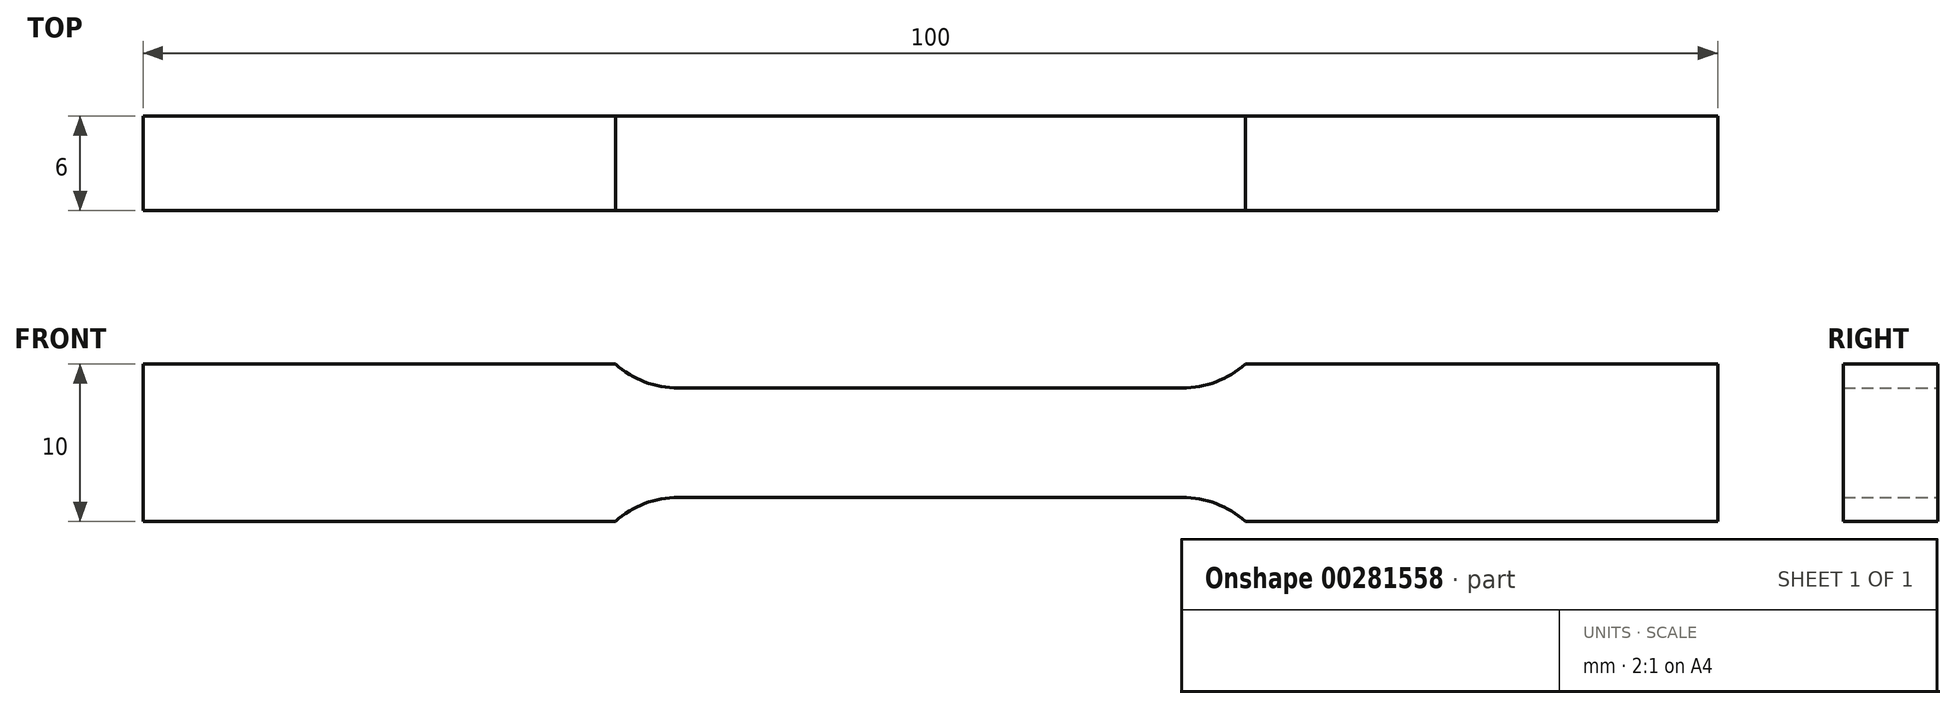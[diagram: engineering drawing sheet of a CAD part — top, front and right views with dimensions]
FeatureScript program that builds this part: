
annotation { "Feature Type Name" : "Feature", "Feature Type Description" : "" }
export const myFeature = defineFeature(function(context is Context, id is Id, definition is map)
    precondition{}
    {
        {
            var Q0;
            Q0=qCreatedBy(makeId("Front.planeOp"),FACE);
            var sketch = newSketch(context, id + "F0", { "sketchPlane" : qUnion([Q0])});
            skLineSegment(sketch, "E0", {"start": v(0, 3.47) * mm, "end": v(16, 3.47) * mm});
            skArc(sketch, "E1", {"start": v(16, 3.47) * mm, "mid": v(18.14, 3.87) * mm, "end": v(20, 5) * mm});
            skLineSegment(sketch, "E2", {"start": v(20, 5) * mm, "end": v(50, 5) * mm});
            skLineSegment(sketch, "E3", {"start": v(50, 5) * mm, "end": v(50, 0) * mm});
            skLineSegment(sketch, "E4.MirrorCS", {"start": v(0, -3.47) * mm, "end": v(16, -3.47) * mm});
            skLineSegment(sketch, "E5.MirrorCS", {"start": v(50, -5) * mm, "end": v(50, 0) * mm});
            skLineSegment(sketch, "E6.MirrorCS", {"start": v(20, -5) * mm, "end": v(50, -5) * mm});
            skArc(sketch, "E7.MirrorCS", {"start": v(16, -3.47) * mm, "mid": v(18.14, -3.87) * mm, "end": v(20, -5) * mm});
            skArc(sketch, "E8.MirrorCS", {"start": v(-16, -3.47) * mm, "mid": v(-18.14, -3.87) * mm, "end": v(-20, -5) * mm});
            skArc(sketch, "E9.MirrorCS", {"start": v(-16, 3.47) * mm, "mid": v(-18.14, 3.87) * mm, "end": v(-20, 5) * mm});
            skLineSegment(sketch, "E10.MirrorCS", {"start": v(-20, -5) * mm, "end": v(-50, -5) * mm});
            skLineSegment(sketch, "E11.MirrorCS", {"start": v(-20, 5) * mm, "end": v(-50, 5) * mm});
            skLineSegment(sketch, "E12.MirrorCS", {"start": v(-50, -5) * mm, "end": v(-50, 0) * mm});
            skLineSegment(sketch, "E13.MirrorCS", {"start": v(0, -3.47) * mm, "end": v(-16, -3.47) * mm});
            skLineSegment(sketch, "E14.MirrorCS", {"start": v(-50, 5) * mm, "end": v(-50, 0) * mm});
            skLineSegment(sketch, "E15.MirrorCS", {"start": v(0, 3.47) * mm, "end": v(-16, 3.47) * mm});
            skSolve(sketch);
        }
        {
            var Q0;
            Q0=makeQuery(id+"F0.imprint","IMPRINT",FACE,{"disambiguationData":[TD([[makeQuery(id+"F0.imprint","IMPRINT",EDGE,{"derivedFrom":sQuery(id+"F0.wireOp",EDGE,"E0")}),-1.0]])]});
            extrude(context, id + "F1", {"entities" : qUnion([Q0]), "endBound" : BoundingType.SYMMETRIC, "depth" : 6 * mm});
        }
    });
